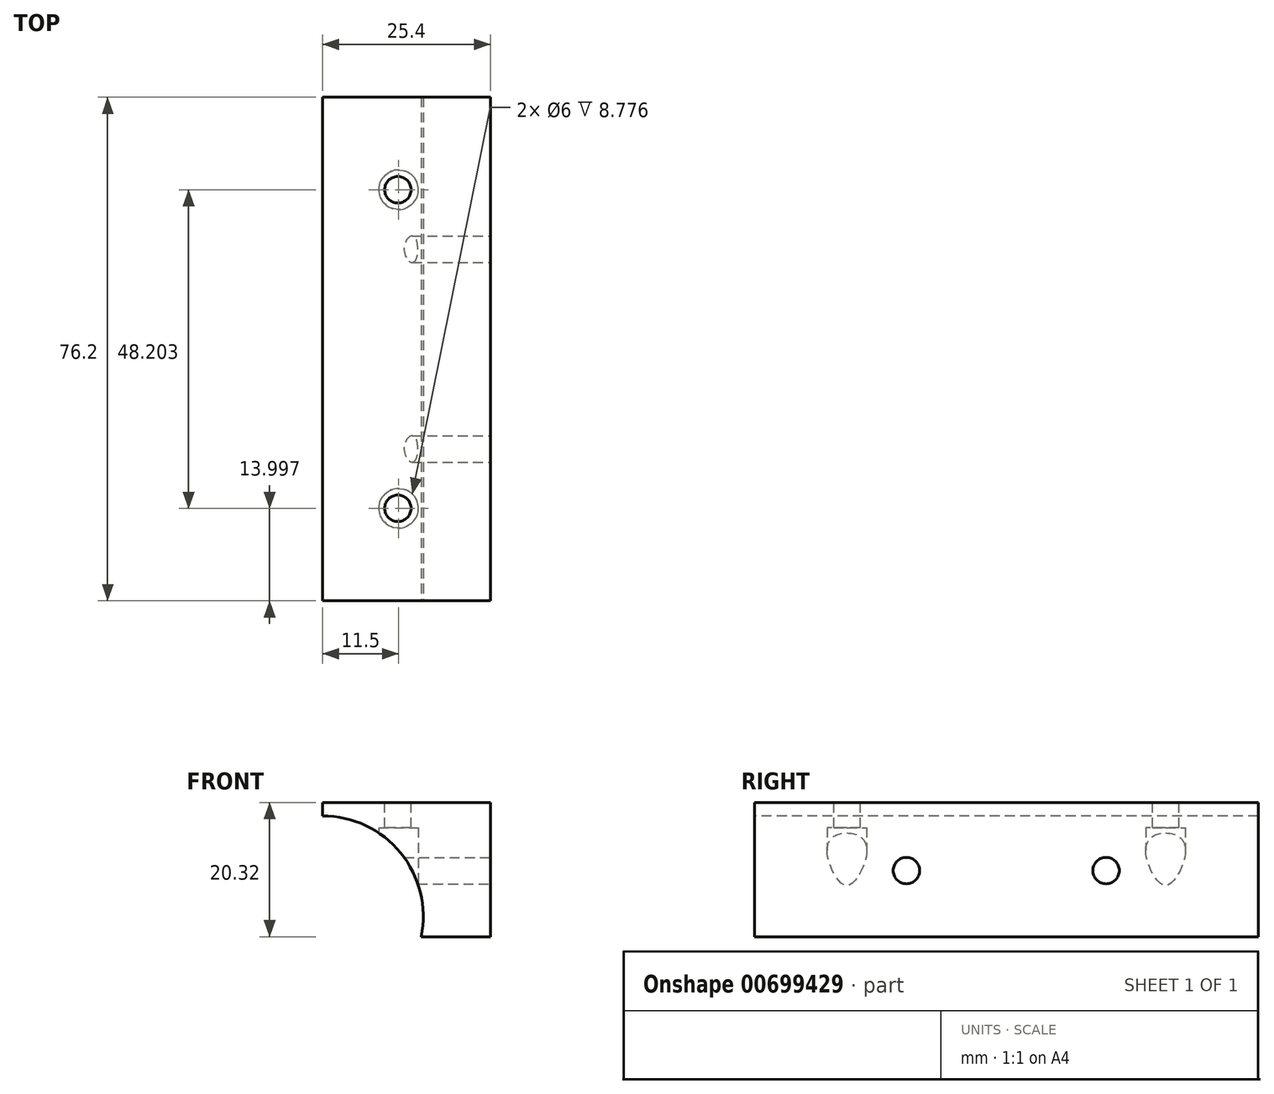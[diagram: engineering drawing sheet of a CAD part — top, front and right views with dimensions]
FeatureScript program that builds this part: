
annotation { "Feature Type Name" : "Feature", "Feature Type Description" : "" }
export const myFeature = defineFeature(function(context is Context, id is Id, definition is map)
    precondition{}
    {
        {
            var Q0;
            Q0=qCreatedBy(makeId("Front.planeOp"),FACE);
            var sketch = newSketch(context, id + "F0", { "sketchPlane" : qUnion([Q0])});
            skLineSegment(sketch, "E0.bottom", {"start": v(0, 20.32) * mm, "end": v(25.4, 20.32) * mm});
            skLineSegment(sketch, "E0.top", {"start": v(0, 0) * mm, "end": v(25.4, 0) * mm});
            skLineSegment(sketch, "E0.left", {"start": v(0, 20.32) * mm, "end": v(0, 0) * mm});
            skLineSegment(sketch, "E0.right", {"start": v(25.4, 20.32) * mm, "end": v(25.4, 0) * mm});
            skSolve(sketch);
        }
        {
            var Q0;
            Q0=makeQuery(id+"F0.imprint","IMPRINT",FACE,{"disambiguationData":[TD([[makeQuery(id+"F0.imprint","IMPRINT",EDGE,{"derivedFrom":sQuery(id+"F0.wireOp",EDGE,"E0.bottom")}),-1.0]])]});
            extrude(context, id + "F1", {"entities" : qUnion([Q0]), "depth" : 76.2 * mm, "offsetDistance" : 25.4 * mm});
        }
        {
            var Q0;
            Q0=makeQuery(id+"F1.opExtrude","CAP_FACE",FACE,{"disambiguationData":[OSD([sQuery(id+"F0.wireOp",EDGE,"E0.bottom"),sQuery(id+"F0.wireOp",EDGE,"E0.top"),sQuery(id+"F0.wireOp",EDGE,"E0.left"),sQuery(id+"F0.wireOp",EDGE,"E0.right")])],"isStart":false});
            var sketch = newSketch(context, id + "F2", { "sketchPlane" : qUnion([Q0])});
            skCircle(sketch, "E1", {"center": v(0, 3.05) * mm, "radius": 15.24 * mm});
            skSolve(sketch);
        }
        {
            var Q0;
            Q0 = qSketchRegion(id + "F2", true);
            extrude(context, id + "F3", {"entities" : qUnion([Q0]), "operationType" : NewBodyOperationType.REMOVE, "oppositeDirection" : true, "depth" : 76.2 * mm, "offsetDistance" : 25.4 * mm});
        }
        {
            var Q0;
            Q0=makeQuery(id+"F1.opExtrude","SWEPT_FACE",FACE,{"disambiguationData":[OSD([sQuery(id+"F0.wireOp",EDGE,"E0.bottom")])]});
            var sketch = newSketch(context, id + "F4", { "sketchPlane" : qUnion([Q0])});
            skCircle(sketch, "E2", {"center": v(11.4, -14) * mm, "radius": 2 * mm});
            skCircle(sketch, "E3", {"center": v(11.4, -62.2) * mm, "radius": 2 * mm});
            skSolve(sketch);
        }
        {
            var Q0;
            Q0 = qSketchRegion(id + "F4", true);
            extrude(context, id + "F5", {"entities" : qUnion([Q0]), "operationType" : NewBodyOperationType.REMOVE, "oppositeDirection" : true, "depth" : 25 * mm, "offsetDistance" : 25 * mm});
        }
        {
            var Q0;
            Q0=qCreatedBy(makeId("Top.planeOp"),FACE);
            var sketch = newSketch(context, id + "F6", { "sketchPlane" : qUnion([Q0])});
            skCircle(sketch, "E4", {"center": v(11.5, -14) * mm, "radius": 3 * mm});
            skCircle(sketch, "E5", {"center": v(11.5, -62.2) * mm, "radius": 3 * mm});
            skSolve(sketch);
        }
        {
            var Q0;
            Q0=makeQuery(id+"F6.imprint","IMPRINT",FACE,{"disambiguationData":[TD([[makeQuery(id+"F6.imprint","IMPRINT",EDGE,{"derivedFrom":sQuery(id+"F6.wireOp",EDGE,"E4")}),1.0]])]});
            var Q1;
            Q1=makeQuery(id+"F6.imprint","IMPRINT",FACE,{"disambiguationData":[TD([[makeQuery(id+"F6.imprint","IMPRINT",EDGE,{"derivedFrom":sQuery(id+"F6.wireOp",EDGE,"E5")}),1.0]])]});
            extrude(context, id + "F7", {"entities" : qUnion([Q0, Q1]), "operationType" : NewBodyOperationType.REMOVE, "depth" : 16.5 * mm, "offsetDistance" : 25 * mm});
        }
        {
            var Q0;
            Q0=makeQuery(id+"F1.opExtrude","SWEPT_FACE",FACE,{"disambiguationData":[OSD([sQuery(id+"F0.wireOp",EDGE,"E0.right")])]});
            var sketch = newSketch(context, id + "F8", { "sketchPlane" : qUnion([Q0])});
            skCircle(sketch, "E6", {"center": v(-23, 10) * mm, "radius": 2 * mm});
            skCircle(sketch, "E7", {"center": v(-53.2, 10) * mm, "radius": 2 * mm});
            skSolve(sketch);
        }
        {
            var Q0;
            Q0=makeQuery(id+"F8.imprint","IMPRINT",FACE,{"disambiguationData":[TD([[makeQuery(id+"F8.imprint","IMPRINT",EDGE,{"derivedFrom":sQuery(id+"F8.wireOp",EDGE,"E6")}),1.0]])]});
            var Q1;
            Q1=makeQuery(id+"F8.imprint","IMPRINT",FACE,{"disambiguationData":[TD([[makeQuery(id+"F8.imprint","IMPRINT",EDGE,{"derivedFrom":sQuery(id+"F8.wireOp",EDGE,"E7")}),1.0]])]});
            extrude(context, id + "F9", {"entities" : qUnion([Q0, Q1]), "operationType" : NewBodyOperationType.REMOVE, "oppositeDirection" : true, "depth" : 25 * mm, "offsetDistance" : 25 * mm});
        }
    });
